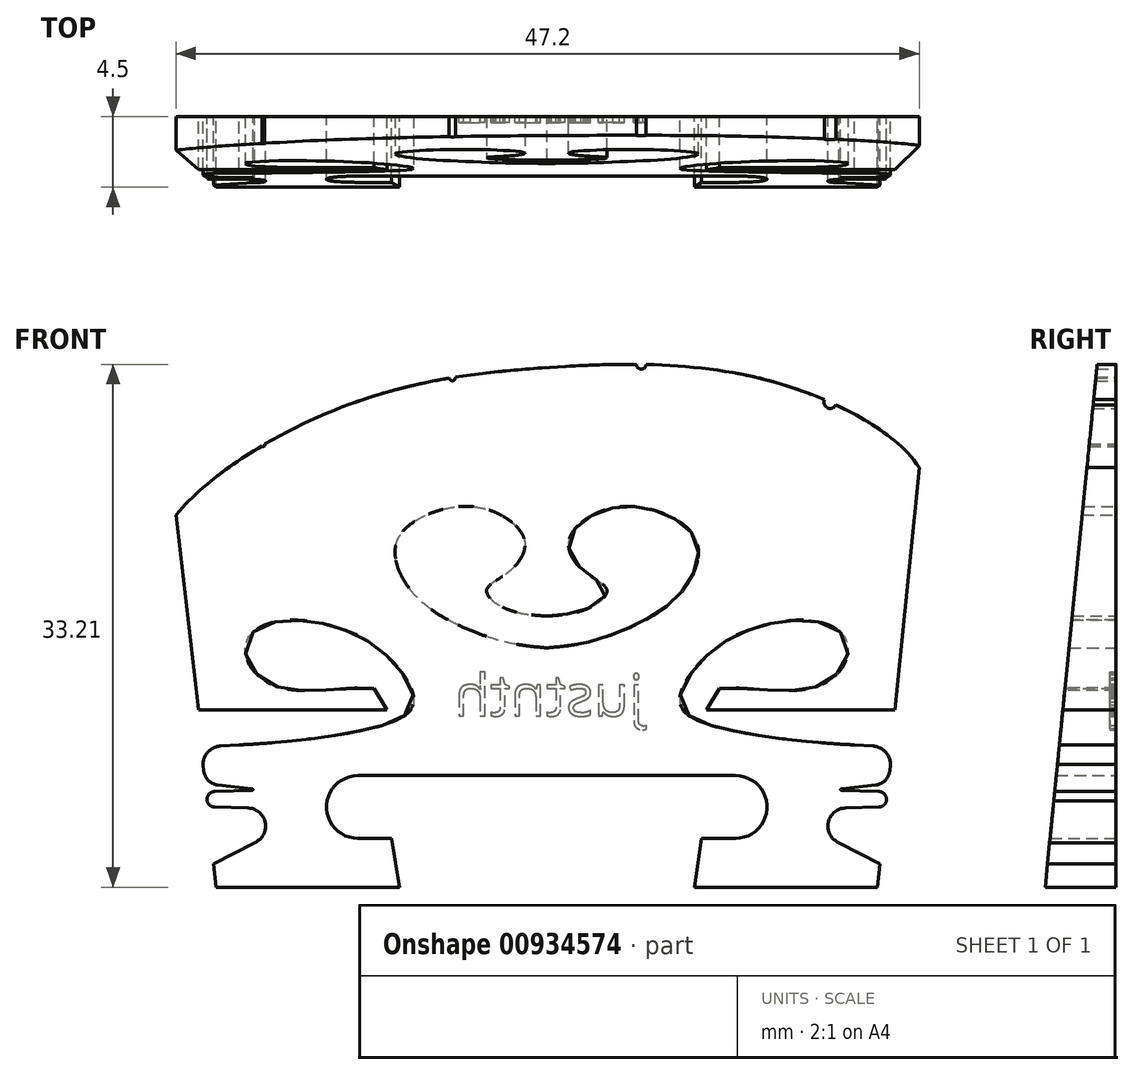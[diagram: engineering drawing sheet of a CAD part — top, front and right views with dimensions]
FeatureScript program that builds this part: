
annotation { "Feature Type Name" : "Feature", "Feature Type Description" : "" }
export const myFeature = defineFeature(function(context is Context, id is Id, definition is map)
    precondition{}
    {
        {
            var Q0;
            Q0=qCreatedBy(makeId("Front.planeOp"),FACE);
            var sketch = newSketch(context, id + "F0", { "sketchPlane" : qUnion([Q0])});
            skFitSpline(sketch, "E0", {"points": [v(-23.54, 23.66) * mm, v(-12.1, 30.83) * mm, v(0, 33) * mm, v(13.95, 32.22) * mm, v(23.66, 26.65) * mm], "startDerivative": vector(29.69, 35.16) * mm, "endDerivative": vector(19.16, -29.67) * mm});
            skLineSegment(sketch, "E1", {"start": v(9.82, 3.09) * mm, "end": v(12, 3.1) * mm});
            skLineSegment(sketch, "E2", {"start": v(12, 7.1) * mm, "end": v(0, 7.1) * mm});
            skArc(sketch, "E3.filletArc", {"start": v(12, 3.1) * mm, "mid": v(14, 5.1) * mm, "end": v(12, 7.1) * mm});
            skLineSegment(sketch, "E4", {"start": v(21, 0) * mm, "end": v(21.16, 1.5) * mm});
            skPoint(sketch, "E5.visualSharp", {"position": v(11.23, 5.08) * mm});
            skFitSpline(sketch, "E6", {"points": [v(0, 15.2) * mm, v(4, 15.99) * mm, v(8.17, 18.33) * mm, v(9.57, 21.81) * mm, v(7.19, 23.82) * mm, v(3.6, 23.93) * mm, v(1.4, 21.97) * mm, v(2.5, 19.96) * mm, v(3.82, 18.86) * mm, v(2.74, 17.76) * mm, v(0, 17.22) * mm], "startDerivative": vector(53.54, 4.7) * mm, "endDerivative": vector(-27.32, -1.62) * mm});
            skFitSpline(sketch, "E7.MirrorCS", {"points": [v(0, 15.2) * mm, v(-4, 15.99) * mm, v(-8.17, 18.33) * mm, v(-9.57, 21.81) * mm, v(-7.19, 23.82) * mm, v(-3.6, 23.93) * mm, v(-1.4, 21.97) * mm, v(-2.5, 19.96) * mm, v(-3.82, 18.86) * mm, v(-2.74, 17.76) * mm, v(0, 17.22) * mm], "startDerivative": vector(-53.54, 4.7) * mm, "endDerivative": vector(27.32, -1.62) * mm});
            skLineSegment(sketch, "E8.MirrorCS", {"start": v(-12, 7.1) * mm, "end": v(0, 7.1) * mm});
            skArc(sketch, "E9.MirrorCS", {"start": v(-12.01, 3.1) * mm, "mid": v(-14, 5.1) * mm, "end": v(-12, 7.1) * mm});
            skLineSegment(sketch, "E10.MirrorCS", {"start": v(-9.85, 3.08) * mm, "end": v(-12.01, 3.1) * mm});
            skLineSegment(sketch, "E11", {"start": v(-21.16, 1.5) * mm, "end": v(-21, 0) * mm});
            skFitSpline(sketch, "E12.MirrorCS", {"points": [v(10.96, 12.63) * mm, v(17.29, 12.8) * mm, v(19.14, 15.37) * mm, v(17, 16.9) * mm, v(12.21, 16.08) * mm, v(9.91, 14.46) * mm, v(8.57, 12.54) * mm, v(9.18, 10.8) * mm, v(19.55, 9.04) * mm], "startDerivative": vector(28.37, 3.52) * mm, "endDerivative": vector(23.7, -0.72) * mm});
            skLineSegment(sketch, "E13.MirrorCS", {"start": v(10.96, 12.63) * mm, "end": v(10.14, 11.25) * mm});
            skLineSegment(sketch, "E14", {"start": v(-18, 62.47) * mm, "end": v(-18, 22.93) * mm, "construction": true});
            skLineSegment(sketch, "E15", {"start": v(6, 60.56) * mm, "end": v(6, 29.37) * mm, "construction": true});
            skLineSegment(sketch, "E16", {"start": v(18, 61.03) * mm, "end": v(18, 25.82) * mm, "construction": true});
            skLineSegment(sketch, "E17", {"start": v(-6, 62.47) * mm, "end": v(-6, 28.49) * mm, "construction": true});
            skCircle(sketch, "E18", {"center": v(-18, 28.08) * mm, "radius": 0.1 * mm});
            skCircle(sketch, "E19", {"center": v(-6, 32.36) * mm, "radius": 0.2 * mm});
            skCircle(sketch, "E20", {"center": v(18, 30.8) * mm, "radius": 0.4 * mm});
            skCircle(sketch, "E21", {"center": v(6, 33.2) * mm, "radius": 0.3 * mm});
            skLineSegment(sketch, "E22", {"start": v(23.66, 26.65) * mm, "end": v(22.12, 11.25) * mm});
            skLineSegment(sketch, "E23", {"start": v(22.12, 11.25) * mm, "end": v(10.14, 11.25) * mm});
            skLineSegment(sketch, "E24", {"start": v(21.16, 1.5) * mm, "end": v(18.56, 2.82) * mm});
            skLineSegment(sketch, "E25", {"start": v(20.7, 8.97) * mm, "end": v(19.55, 9.04) * mm});
            skLineSegment(sketch, "E26", {"start": v(18.96, 5.03) * mm, "end": v(21.1, 5.08) * mm});
            skArc(sketch, "E27", {"start": v(18.96, 5.03) * mm, "mid": v(17.86, 4.1) * mm, "end": v(18.56, 2.82) * mm});
            skPoint(sketch, "E28.visualSharp", {"position": v(21.52, 5.1) * mm});
            skArc(sketch, "E28.filletArc", {"start": v(21.1, 5.08) * mm, "mid": v(21.4, 5.2) * mm, "end": v(21.57, 5.47) * mm});
            skLineSegment(sketch, "E29", {"start": v(21.57, 5.47) * mm, "end": v(21.58, 5.52) * mm});
            skArc(sketch, "E30.filletArc", {"start": v(21.58, 5.52) * mm, "mid": v(21.45, 5.9) * mm, "end": v(21.08, 6.07) * mm});
            skArc(sketch, "E31.filletArc", {"start": v(21.83, 7.8) * mm, "mid": v(21.5, 8.6) * mm, "end": v(20.7, 8.97) * mm});
            skLineSegment(sketch, "E32", {"start": v(21.08, 6.07) * mm, "end": v(18.71, 6.15) * mm});
            skFitSpline(sketch, "E33.MirrorCS", {"points": [v(-10.96, 12.63) * mm, v(-17.29, 12.8) * mm, v(-19.14, 15.37) * mm, v(-17, 16.9) * mm, v(-12.21, 16.08) * mm, v(-9.91, 14.46) * mm, v(-8.57, 12.54) * mm, v(-9.18, 10.8) * mm, v(-19.55, 9.04) * mm], "startDerivative": vector(-28.37, 3.52) * mm, "endDerivative": vector(-23.7, -0.72) * mm});
            skLineSegment(sketch, "E34.MirrorCS", {"start": v(-10.96, 12.63) * mm, "end": v(-10.14, 11.25) * mm});
            skLineSegment(sketch, "E35.MirrorCS", {"start": v(-22.12, 11.25) * mm, "end": v(-10.14, 11.25) * mm});
            skLineSegment(sketch, "E36.MirrorCS", {"start": v(-18.96, 5.03) * mm, "end": v(-21.1, 5.08) * mm});
            skArc(sketch, "E37.MirrorCS", {"start": v(-18.96, 5.03) * mm, "mid": v(-17.86, 4.1) * mm, "end": v(-18.56, 2.82) * mm});
            skLineSegment(sketch, "E38.MirrorCS", {"start": v(-21.16, 1.5) * mm, "end": v(-18.56, 2.82) * mm});
            skLineSegment(sketch, "E39", {"start": v(-22.12, 11.25) * mm, "end": v(-23.54, 23.66) * mm});
            skLineSegment(sketch, "E40", {"start": v(18.7, 6.25) * mm, "end": v(20.9, 6.49) * mm});
            skLineSegment(sketch, "E41", {"start": v(21.78, 7.37) * mm, "end": v(21.83, 7.8) * mm});
            skArc(sketch, "E42.filletArc", {"start": v(20.9, 6.49) * mm, "mid": v(21.5, 6.77) * mm, "end": v(21.78, 7.37) * mm});
            skPoint(sketch, "E43.visualSharp", {"position": v(18, 6.17) * mm});
            skArc(sketch, "E43.filletArc", {"start": v(18.7, 6.25) * mm, "mid": v(18.66, 6.2) * mm, "end": v(18.71, 6.15) * mm});
            skLineSegment(sketch, "E44.MirrorCS", {"start": v(-20.7, 8.97) * mm, "end": v(-19.55, 9.04) * mm});
            skArc(sketch, "E45.MirrorCS", {"start": v(-21.83, 7.8) * mm, "mid": v(-21.5, 8.6) * mm, "end": v(-20.7, 8.97) * mm});
            skLineSegment(sketch, "E46.MirrorCS", {"start": v(-21.78, 7.37) * mm, "end": v(-21.83, 7.8) * mm});
            skArc(sketch, "E47.MirrorCS", {"start": v(-20.9, 6.49) * mm, "mid": v(-21.5, 6.77) * mm, "end": v(-21.78, 7.37) * mm});
            skLineSegment(sketch, "E48.MirrorCS", {"start": v(-18.7, 6.25) * mm, "end": v(-20.9, 6.49) * mm});
            skArc(sketch, "E49.MirrorCS", {"start": v(-18.7, 6.25) * mm, "mid": v(-18.66, 6.2) * mm, "end": v(-18.71, 6.15) * mm});
            skLineSegment(sketch, "E50.MirrorCS", {"start": v(-21.08, 6.07) * mm, "end": v(-18.71, 6.15) * mm});
            skArc(sketch, "E51.MirrorCS", {"start": v(-21.58, 5.52) * mm, "mid": v(-21.45, 5.9) * mm, "end": v(-21.08, 6.07) * mm});
            skArc(sketch, "E52.MirrorCS", {"start": v(-21.1, 5.08) * mm, "mid": v(-21.4, 5.2) * mm, "end": v(-21.57, 5.47) * mm});
            skLineSegment(sketch, "E53.MirrorCS", {"start": v(-21.57, 5.47) * mm, "end": v(-21.58, 5.52) * mm});
            skLineSegment(sketch, "E54", {"start": v(-9.85, 3.08) * mm, "end": v(-9.36, 0) * mm});
            skLineSegment(sketch, "E55", {"start": v(-9.36, 0) * mm, "end": v(-21, 0) * mm});
            skLineSegment(sketch, "E56", {"start": v(9.39, 0) * mm, "end": v(21, 0) * mm});
            skLineSegment(sketch, "E57", {"start": v(9.82, 3.09) * mm, "end": v(9.39, 0) * mm});
            skSolve(sketch);
        }
        {
            var Q0;
            {var subQ1=sQuery(id+"F0.wireOp",EDGE,"E0");Q0=makeQuery(id+"F0.imprint","IMPRINT",FACE,{"disambiguationData":[TD([[makeQuery(id+"F0.imprint","IMPRINT",EDGE,{"derivedFrom":subQ1}),-1.0]])]});}
            extrude(context, id + "F1", {"entities" : qUnion([Q0]), "depth" : 4.5 * mm, "offsetDistance" : 25.4 * mm});
        }
        {
            var Q0;
            Q0=qCreatedBy(makeId("Right.planeOp"),FACE);
            var sketch = newSketch(context, id + "F2", { "sketchPlane" : qUnion([Q0])});
            skLineSegment(sketch, "E58", {"start": v(-1.2, 78.1) * mm, "end": v(-1.2, 1.9) * mm});
            skLineSegment(sketch, "E59", {"start": v(12.46, 33.21) * mm, "end": v(-25.03, 33.21) * mm});
            skLineSegment(sketch, "E60", {"start": v(-4.5, -2.46) * mm, "end": v(-4.5, 45.63) * mm});
            skLineSegment(sketch, "E61", {"start": v(-1.2, 33.21) * mm, "end": v(-4.5, 0) * mm});
            skLineSegment(sketch, "E62", {"start": v(-4.5, 0) * mm, "end": v(-9, 0) * mm});
            skLineSegment(sketch, "E63", {"start": v(-9, 0) * mm, "end": v(-7.85, 33.21) * mm});
            skLineSegment(sketch, "E64", {"start": v(-7.85, 33.21) * mm, "end": v(-1.2, 33.21) * mm});
            skLineSegment(sketch, "E65.top", {"start": v(-7.85, 40.77) * mm, "end": v(-1.2, 40.77) * mm});
            skLineSegment(sketch, "E65.left", {"start": v(-7.85, 33.21) * mm, "end": v(-7.85, 40.77) * mm});
            skLineSegment(sketch, "E65.right", {"start": v(-1.2, 33.21) * mm, "end": v(-1.2, 40.77) * mm});
            skSolve(sketch);
        }
        {
            var Q0;
            {var subQ4=sQuery(id+"F2.wireOp",EDGE,"E62");Q0=makeQuery(id+"F2.imprint","IMPRINT",FACE,{"disambiguationData":[TD([[makeQuery(id+"F2.imprint","IMPRINT",EDGE,{"derivedFrom":subQ4}),-1.0]])]});}
            var Q1;
            {var subQ0=sQuery(id+"F2.wireOp",EDGE,"E61");Q1=makeQuery(id+"F2.imprint","IMPRINT",FACE,{"disambiguationData":[TD([[makeQuery(id+"F2.imprint","IMPRINT",EDGE,{"derivedFrom":subQ0}),-1.0]])]});}
            var Q2;
            {var subQ0=sQuery(id+"F2.wireOp",EDGE,"E65.left");Q2=makeQuery(id+"F2.imprint","IMPRINT",FACE,{"disambiguationData":[TD([[makeQuery(id+"F2.imprint","IMPRINT",EDGE,{"derivedFrom":subQ0}),-1.0]])]});}
            var Q3;
            {var subQ0=sQuery(id+"F2.wireOp",EDGE,"E59");var subQ5=sQuery(id+"F2.wireOp",EDGE,"E60");var subQ6=makeQuery(id+"F2.imprint","INTERSECT",VERTEX,{"derivedFrom":[subQ0,subQ5]});Q3=makeQuery(id+"F2.imprint","IMPRINT",FACE,{"disambiguationData":[TD([[makeQuery(id+"F2.imprint","IMPRINT",EDGE,{"disambiguationData":[TD([[subQ6,-1.0]])],"derivedFrom":subQ5}),-1.0]])]});}
            extrude(context, id + "F3", {"entities" : qUnion([Q0, Q1, Q2, Q3]), "operationType" : NewBodyOperationType.REMOVE, "endBound" : BoundingType.SYMMETRIC, "depth" : 60 * mm, "offsetDistance" : 25.4 * mm});
        }
        {
            var Q0;
            Q0=makeQuery(id+"F1.opExtrude","CAP_FACE",FACE,{"disambiguationData":[OSD([sQuery(id+"F0.wireOp",EDGE,"E0"),sQuery(id+"F0.wireOp",EDGE,"e4hmPngl-bTp4-2FKX-qq5L-C8yQQZpSV2t0"),sQuery(id+"F0.wireOp",EDGE,"m3C9ovOK-315E-PIzk-nrXY-3GBNYPGDzf1G"),sQuery(id+"F0.wireOp",EDGE,"E1"),sQuery(id+"F0.wireOp",EDGE,"E2"),sQuery(id+"F0.wireOp",EDGE,"E3.filletArc"),sQuery(id+"F0.wireOp",EDGE,"E4"),sQuery(id+"F0.wireOp",EDGE,"E6"),sQuery(id+"F0.wireOp",EDGE,"E7.MirrorCS"),sQuery(id+"F0.wireOp",EDGE,"E8.MirrorCS"),sQuery(id+"F0.wireOp",EDGE,"E9.MirrorCS"),sQuery(id+"F0.wireOp",EDGE,"E10.MirrorCS"),sQuery(id+"F0.wireOp",EDGE,"369ba2a7-3018-45a9-8760-523ebc0fda910.MirrorCS"),sQuery(id+"F0.wireOp",EDGE,"99c2ba22-9a41-4c2a-bd8a-ffb563d2db590.MirrorCS"),sQuery(id+"F0.wireOp",EDGE,"E11"),sQuery(id+"F0.wireOp",EDGE,"sNap6CoO-IBVS-i1IY-ntVr-FjdyHk4U1fLk"),sQuery(id+"F0.wireOp",EDGE,"Q49nbHIn-tZww-OQF0-PmV4-upVZ2FfT46EY"),sQuery(id+"F0.wireOp",EDGE,"cacc4af9-22af-473b-8ac6-10344cc65f12.filletArc"),sQuery(id+"F0.wireOp",EDGE,"b2179551-9911-4662-ab98-ed61c98f1fae0.MirrorCS"),sQuery(id+"F0.wireOp",EDGE,"WLDu3wvJ-hjGy-TZ6D-QxCG-5IQINUcYNDWe"),sQuery(id+"F0.wireOp",EDGE,"c432bdc4-3a2f-4fb0-98df-54dfc78423e7.filletArc"),sQuery(id+"F0.wireOp",EDGE,"686801cf-beb7-4a0b-9bdc-b307e84039be.filletArc"),sQuery(id+"F0.wireOp",EDGE,"xwyop2li-xI9W-UFQn-VAwa-afb1EGiimQMJ"),sQuery(id+"F0.wireOp",EDGE,"5a9beed9-85af-4595-b0f8-0b7d7c26e17c"),sQuery(id+"F0.wireOp",EDGE,"bzGZhi7p-2t2n-dACa-pQoM-uhUXtXE2D66O"),sQuery(id+"F0.wireOp",EDGE,"yywPAmDP-Yir0-P9Cb-WB6Q-Zl7V1TjRpGde"),sQuery(id+"F0.wireOp",EDGE,"E12.MirrorCS"),sQuery(id+"F0.wireOp",EDGE,"E13.MirrorCS"),sQuery(id+"F0.wireOp",EDGE,"PqBrF7gv-Diou-TzOB-6hR5-WF0VOCTdd9Ml"),sQuery(id+"F0.wireOp",EDGE,"irIPY5CA-CWUD-HGs8-Lafv-b9PyqiYwdKW4"),sQuery(id+"F0.wireOp",EDGE,"N699qDvk-ju4z-pMcA-En7K-C2CTM2OkSit7"),sQuery(id+"F0.wireOp",EDGE,"uBNGByd7-gyzj-997R-8Wxi-t9WqYOMEbmyB"),sQuery(id+"F0.wireOp",EDGE,"5093e992-0bc9-46ed-b494-589bb84dc8b9.filletArc"),sQuery(id+"F0.wireOp",EDGE,"d6a4b0fc-a71b-4a5d-b080-7cea932b6cd3.filletArc"),sQuery(id+"F0.wireOp",EDGE,"E18"),sQuery(id+"F0.wireOp",EDGE,"E19"),sQuery(id+"F0.wireOp",EDGE,"E20"),sQuery(id+"F0.wireOp",EDGE,"E21"),sQuery(id+"F0.wireOp",EDGE,"zmxQx3sE-Abgh-AzOG-xcvg-COG9eKqwMoW1"),sQuery(id+"F0.wireOp",EDGE,"6rnEQyg1-XuVb-NNO3-yQ0c-2cqNmvtJoFj3"),sQuery(id+"F0.wireOp",EDGE,"a740fce4-74ea-4a46-8614-070f5a65ce19.filletArc"),sQuery(id+"F0.wireOp",EDGE,"47d1662d-1cdc-404f-a2f1-9a71518fff21.filletArc"),sQuery(id+"F0.wireOp",EDGE,"x81WzDIV-gmfL-YwrE-CoO7-FSQeT6FRB7PQ"),sQuery(id+"F0.wireOp",EDGE,"GdfCoyAb-hPPH-aXcI-0p9N-VLlFjwOMujNR"),sQuery(id+"F0.wireOp",EDGE,"af57f127-2944-47e9-8a9b-73b34502bf92.filletArc"),sQuery(id+"F0.wireOp",EDGE,"19e7adce-8ca8-4fdb-b1fc-b8dd92e8bc45.filletArc")])],"isStart":true});
            var sketch = newSketch(context, id + "F4", { "sketchPlane" : qUnion([Q0])});
            skText(sketch, "E66", { "text": "justnth", "fontName": "OpenSans-Regular.ttf"});
            const initialGuessF4  = {"E66": [-0.00615, 0.01088, 1, 0, 0.00264]};
            skSetInitialGuess(sketch, initialGuessF4);
            skSolve(sketch);
        }
        {
            var Q0;
            Q0=qSketchRegion(id+"F4",true);
            extrude(context, id + "F5", {"entities" : qUnion([Q0]), "operationType" : NewBodyOperationType.REMOVE, "oppositeDirection" : true, "depth" : 0.4 * mm, "offsetDistance" : 25.4 * mm});
        }
    });
